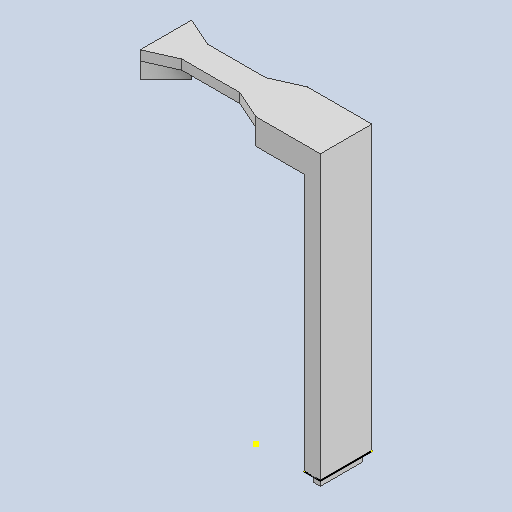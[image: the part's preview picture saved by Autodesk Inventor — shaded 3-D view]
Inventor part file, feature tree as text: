
AUTODESK INVENTOR PART (.ipt)
format: ipt  version: 2025.2 (Build 292293000, 293)  size: 282,112 bytes
history: native  units: mm
features: extrude x5, sketch x5
ambient origin geometry x8: Origin, YZ Plane, XZ Plane, XY Plane, X Axis, Y Axis, Z Axis, Center Point
bodies: Solid1 (feature_tree)
feature tree (10):
  extrude  "Extrusion1"  Depth=20.0mm
  sketch  "Sketch2"  dims[d3=5.0mm d4=0.0mm d5=5.0mm]
  extrude  "Extrusion2"  Depth=5.0mm
  extrude  "Extrusion3"  Depth=1.5mm
  extrude  "Extrusion4"  Depth=13.0mm
  extrude  "Extrusion5"  Depth=3.0mm
  sketch  "Sketch5"  dims[d12=83.0mm d13=0.0mm d14=36.0mm d15=45.0deg d16=5.0mm d17=0.0mm d18=3.0mm d19=0.0mm]
  sketch  "Sketch1"  dims[d0=16.0mm d2=20.0mm]
  sketch  "Sketch3"  dims[d6=80.0mm d7=0.0mm d8=1.5mm]
  sketch  "Sketch4"  dims[d9=1.5mm d11=13.0mm]
